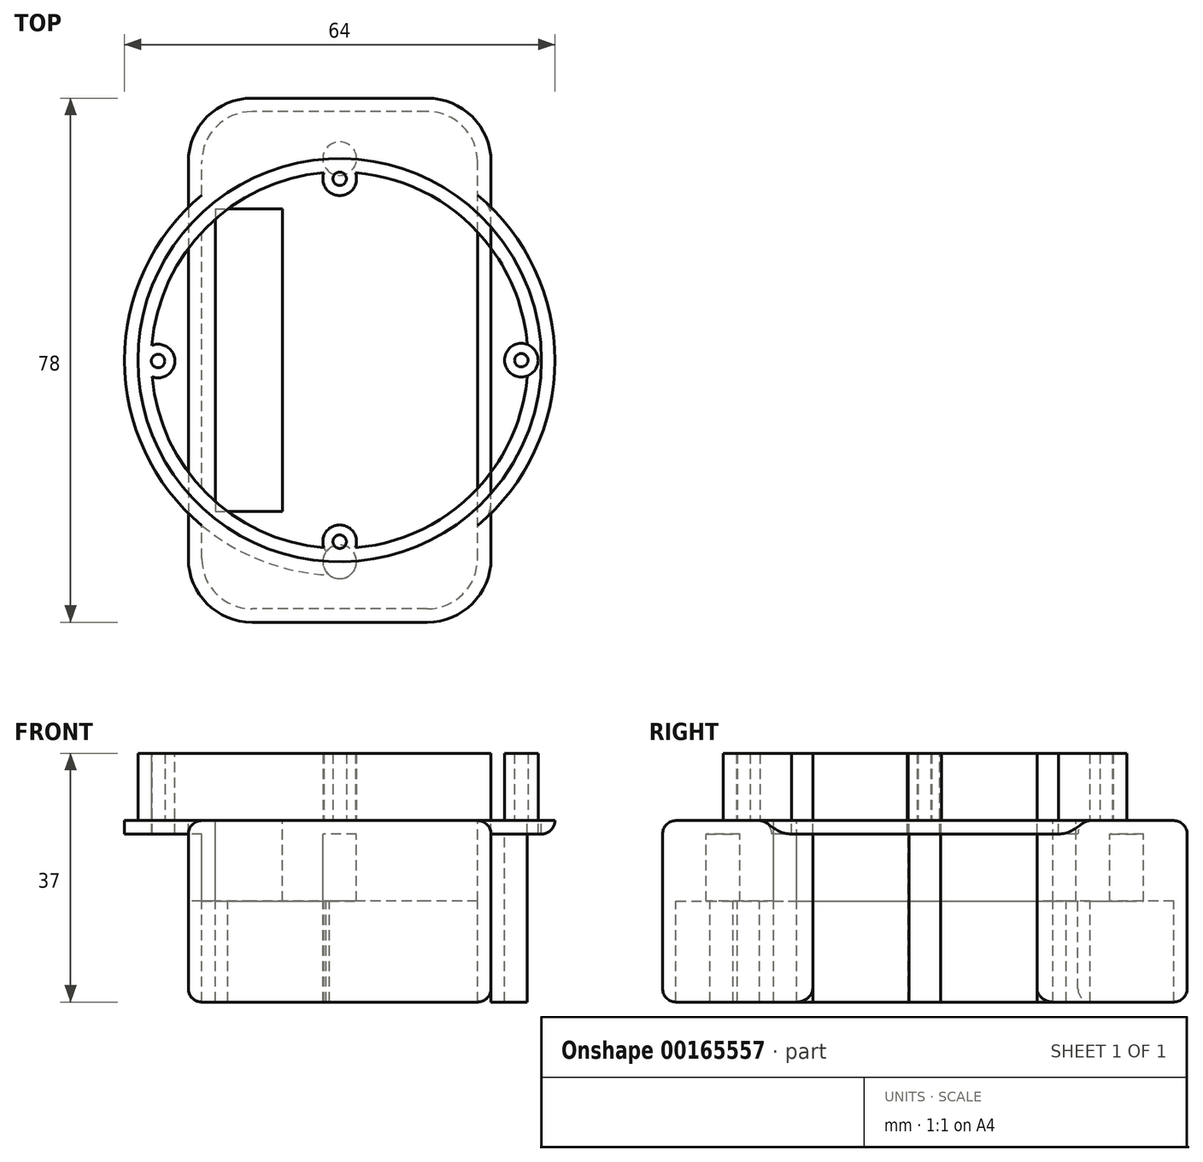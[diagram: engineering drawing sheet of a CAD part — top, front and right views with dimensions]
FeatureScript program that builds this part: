
annotation { "Feature Type Name" : "Feature", "Feature Type Description" : "" }
export const myFeature = defineFeature(function(context is Context, id is Id, definition is map)
    precondition{}
    {
        {
            var Q0;
            Q0=qCreatedBy(makeId("Top.planeOp"),FACE);
            var sketch = newSketch(context, id + "F0", { "sketchPlane" : qUnion([Q0])});
            skCircle(sketch, "E0", {"center": v(0, 0) * mm, "radius": 30 * mm});
            skCircle(sketch, "E1.0", {"center": v(0, 0) * mm, "radius": 28 * mm});
            skLineSegment(sketch, "E2.bottom", {"start": v(13, -37) * mm, "end": v(-13, -37) * mm});
            skLineSegment(sketch, "E2.top", {"start": v(13, 37) * mm, "end": v(-13, 37) * mm});
            skLineSegment(sketch, "E2.left", {"start": v(20.5, -29.5) * mm, "end": v(20.5, 29.5) * mm});
            skLineSegment(sketch, "E2.right", {"start": v(-20.5, -29.5) * mm, "end": v(-20.5, 29.5) * mm});
            skPoint(sketch, "E3.visualSharp", {"position": v(-20.5, 37) * mm});
            skArc(sketch, "E3.filletArc", {"start": v(-13, 37) * mm, "mid": v(-18.3, 34.8) * mm, "end": v(-20.5, 29.5) * mm});
            skPoint(sketch, "E4.visualSharp", {"position": v(20.5, 37) * mm});
            skArc(sketch, "E4.filletArc", {"start": v(20.5, 29.5) * mm, "mid": v(18.3, 34.8) * mm, "end": v(13, 37) * mm});
            skPoint(sketch, "E5.visualSharp", {"position": v(20.5, -37) * mm});
            skArc(sketch, "E5.filletArc", {"start": v(13, -37) * mm, "mid": v(18.3, -34.8) * mm, "end": v(20.5, -29.5) * mm});
            skPoint(sketch, "E6.visualSharp", {"position": v(-20.5, -37) * mm});
            skArc(sketch, "E6.filletArc", {"start": v(-20.5, -29.5) * mm, "mid": v(-18.3, -34.8) * mm, "end": v(-13, -37) * mm});
            skArc(sketch, "E7.0", {"start": v(-22.5, -29.5) * mm, "mid": v(-19.72, -36.22) * mm, "end": v(-13, -39) * mm});
            skLineSegment(sketch, "E7.1", {"start": v(13, -39) * mm, "end": v(-13, -39) * mm});
            skLineSegment(sketch, "E7.2", {"start": v(-22.5, -29.5) * mm, "end": v(-22.5, 29.5) * mm});
            skArc(sketch, "E7.3", {"start": v(13, -39) * mm, "mid": v(19.72, -36.22) * mm, "end": v(22.5, -29.5) * mm});
            skArc(sketch, "E7.4", {"start": v(-13, 39) * mm, "mid": v(-19.72, 36.22) * mm, "end": v(-22.5, 29.5) * mm});
            skLineSegment(sketch, "E7.5", {"start": v(13, 39) * mm, "end": v(-13, 39) * mm});
            skArc(sketch, "E7.6", {"start": v(22.5, 29.5) * mm, "mid": v(19.72, 36.22) * mm, "end": v(13, 39) * mm});
            skLineSegment(sketch, "E7.7", {"start": v(22.5, -29.5) * mm, "end": v(22.5, 29.5) * mm});
            skCircle(sketch, "E8", {"center": v(0, 0) * mm, "radius": 27 * mm, "construction": true});
            skCircle(sketch, "E9", {"center": v(0, -27) * mm, "radius": 2.5 * mm});
            skCircle(sketch, "E10", {"center": v(0, 27) * mm, "radius": 2.5 * mm});
            skCircle(sketch, "E11", {"center": v(-27, -0.12) * mm, "radius": 2.5 * mm});
            skCircle(sketch, "E12", {"center": v(27, 0) * mm, "radius": 2.5 * mm});
            skPoint(sketch, "E12.centerSnap0", {"position": v(20.5, 0) * mm});
            skCircle(sketch, "E13", {"center": v(-27, -0.12) * mm, "radius": 1 * mm});
            skCircle(sketch, "E14", {"center": v(0, 27) * mm, "radius": 1 * mm});
            skCircle(sketch, "E15", {"center": v(0, -27) * mm, "radius": 1 * mm});
            skCircle(sketch, "E16", {"center": v(27, 0) * mm, "radius": 1 * mm});
            skLineSegment(sketch, "E17.top", {"start": v(-18.5, 22.5) * mm, "end": v(-8.5, 22.5) * mm});
            skLineSegment(sketch, "E17.left", {"start": v(-18.5, 0) * mm, "end": v(-18.5, 22.5) * mm});
            skLineSegment(sketch, "E17.right", {"start": v(-8.5, 0) * mm, "end": v(-8.5, 22.5) * mm});
            skLineSegment(sketch, "E18.MirrorCS", {"start": v(-8.5, 0) * mm, "end": v(-8.5, -22.5) * mm});
            skLineSegment(sketch, "E19.MirrorCS", {"start": v(-18.5, 0) * mm, "end": v(-18.5, -22.5) * mm});
            skLineSegment(sketch, "E20.MirrorCS", {"start": v(-18.5, -22.5) * mm, "end": v(-8.5, -22.5) * mm});
            skLineSegment(sketch, "E21", {"start": v(0, 0) * mm, "end": v(0, -30) * mm});
            skCircle(sketch, "E22", {"center": v(0, -30) * mm, "radius": 2.5 * mm});
            skCircle(sketch, "E23", {"center": v(0, 30) * mm, "radius": 2.5 * mm});
            skCircle(sketch, "E24", {"center": v(0, 0) * mm, "radius": 32 * mm});
            skSolve(sketch);
        }
        {
            var Q0;
            {var subQ5=sQuery(id+"F0.wireOp",EDGE,"E17.right");Q0=makeQuery(id+"F0.imprint","IMPRINT",FACE,{"disambiguationData":[TD([[makeQuery(id+"F0.imprint","IMPRINT",EDGE,{"derivedFrom":subQ5}),-1.0]])]});}
            var Q1;
            Q1=makeQuery(id+"F0.imprint","IMPRINT",FACE,{"disambiguationData":[TD([[makeQuery(id+"F0.imprint","IMPRINT",EDGE,{"derivedFrom":sQuery(id+"F0.wireOp",EDGE,"E2.top")}),1.0]])]});
            var Q2;
            Q2=makeQuery(id+"F0.imprint","IMPRINT",FACE,{"disambiguationData":[TD([[makeQuery(id+"F0.imprint","IMPRINT",EDGE,{"derivedFrom":sQuery(id+"F0.wireOp",EDGE,"E2.bottom")}),-1.0]])]});
            var Q3;
            {var subQ1=sQuery(id+"F0.wireOp",EDGE,"E17.left");var subQ3=sQuery(id+"F0.wireOp",EDGE,"E1.0");var subQ4=makeQuery(id+"F0.imprint","INTERSECT",VERTEX,{"derivedFrom":[subQ3,subQ1]});Q3=makeQuery(id+"F0.imprint","IMPRINT",FACE,{"disambiguationData":[TD([[makeQuery(id+"F0.imprint","IMPRINT",EDGE,{"disambiguationData":[TD([[subQ4,-1.0]])],"derivedFrom":subQ3}),1.0]])]});}
            var Q4;
            {var subQ5=sQuery(id+"F0.wireOp",EDGE,"E2.right");var subQ6=sQuery(id+"F0.wireOp",EDGE,"E0");var subQ7=makeQuery(id+"F0.imprint","INTERSECT",VERTEX,{"disambiguationData":[OD(1.0)],"derivedFrom":[subQ6,subQ5]});Q4=makeQuery(id+"F0.imprint","IMPRINT",FACE,{"disambiguationData":[TD([[makeQuery(id+"F0.imprint","IMPRINT",EDGE,{"disambiguationData":[TD([[subQ7,-1.0]])],"derivedFrom":subQ6}),1.0]])]});}
            var Q5;
            {var subQ6=sQuery(id+"F0.wireOp",EDGE,"E0");var subQ11=sQuery(id+"F0.wireOp",EDGE,"E23");var subQ12=makeQuery(id+"F0.imprint","INTERSECT",VERTEX,{"disambiguationData":[OD(1.0)],"derivedFrom":[subQ6,subQ11]});Q5=makeQuery(id+"F0.imprint","IMPRINT",FACE,{"disambiguationData":[TD([[makeQuery(id+"F0.imprint","IMPRINT",EDGE,{"disambiguationData":[TD([[subQ12,-1.0]])],"derivedFrom":subQ6}),1.0]])]});}
            var Q6;
            {var subQ0=sQuery(id+"F0.wireOp",EDGE,"E10");var subQ1=sQuery(id+"F0.wireOp",EDGE,"E1.0");var subQ2=makeQuery(id+"F0.imprint","INTERSECT",VERTEX,{"disambiguationData":[OD(0.0)],"derivedFrom":[subQ1,subQ0]});Q6=makeQuery(id+"F0.imprint","IMPRINT",FACE,{"disambiguationData":[TD([[makeQuery(id+"F0.imprint","IMPRINT",EDGE,{"disambiguationData":[TD([[subQ2,-1.0]])],"derivedFrom":subQ1}),1.0]])]});}
            var Q7;
            {var subQ0=sQuery(id+"F0.wireOp",EDGE,"E23");var subQ1=sQuery(id+"F0.wireOp",EDGE,"E14");var subQ2=makeQuery(id+"F0.imprint","INTERSECT",VERTEX,{"disambiguationData":[OD(0.0)],"derivedFrom":[subQ1,subQ0]});Q7=makeQuery(id+"F0.imprint","IMPRINT",FACE,{"disambiguationData":[TD([[makeQuery(id+"F0.imprint","IMPRINT",EDGE,{"disambiguationData":[TD([[subQ2,1.0]])],"derivedFrom":subQ1}),1.0]])]});}
            var Q8;
            {var subQ0=sQuery(id+"F0.wireOp",EDGE,"E23");var subQ1=sQuery(id+"F0.wireOp",EDGE,"E1.0");var subQ2=makeQuery(id+"F0.imprint","INTERSECT",VERTEX,{"disambiguationData":[OD(1.0)],"derivedFrom":[subQ1,subQ0]});Q8=makeQuery(id+"F0.imprint","IMPRINT",FACE,{"disambiguationData":[TD([[makeQuery(id+"F0.imprint","IMPRINT",EDGE,{"disambiguationData":[TD([[subQ2,-1.0]])],"derivedFrom":subQ1}),-1.0]])]});}
            var Q9;
            {var subQ0=sQuery(id+"F0.wireOp",EDGE,"E10");var subQ1=sQuery(id+"F0.wireOp",EDGE,"E1.0");var subQ2=makeQuery(id+"F0.imprint","INTERSECT",VERTEX,{"disambiguationData":[OD(0.0)],"derivedFrom":[subQ1,subQ0]});Q9=makeQuery(id+"F0.imprint","IMPRINT",FACE,{"disambiguationData":[TD([[makeQuery(id+"F0.imprint","IMPRINT",EDGE,{"disambiguationData":[TD([[subQ2,-1.0]])],"derivedFrom":subQ1}),-1.0]])]});}
            var Q10;
            {var subQ0=sQuery(id+"F0.wireOp",EDGE,"E23");var subQ1=sQuery(id+"F0.wireOp",EDGE,"E0");var subQ2=makeQuery(id+"F0.imprint","INTERSECT",VERTEX,{"disambiguationData":[OD(1.0)],"derivedFrom":[subQ1,subQ0]});Q10=makeQuery(id+"F0.imprint","IMPRINT",FACE,{"disambiguationData":[TD([[makeQuery(id+"F0.imprint","IMPRINT",EDGE,{"disambiguationData":[TD([[subQ2,-1.0]])],"derivedFrom":subQ1}),-1.0]])]});}
            var Q11;
            {var subQ0=sQuery(id+"F0.wireOp",EDGE,"E2.left");var subQ1=sQuery(id+"F0.wireOp",EDGE,"E0");var subQ2=makeQuery(id+"F0.imprint","INTERSECT",VERTEX,{"disambiguationData":[OD(0.0)],"derivedFrom":[subQ1,subQ0]});Q11=makeQuery(id+"F0.imprint","IMPRINT",FACE,{"disambiguationData":[TD([[makeQuery(id+"F0.imprint","IMPRINT",EDGE,{"disambiguationData":[TD([[subQ2,-1.0]])],"derivedFrom":subQ1}),-1.0]])]});}
            var Q12;
            {var subQ5=sQuery(id+"F0.wireOp",EDGE,"E2.left");var subQ6=sQuery(id+"F0.wireOp",EDGE,"E0");var subQ7=makeQuery(id+"F0.imprint","INTERSECT",VERTEX,{"disambiguationData":[OD(0.0)],"derivedFrom":[subQ6,subQ5]});Q12=makeQuery(id+"F0.imprint","IMPRINT",FACE,{"disambiguationData":[TD([[makeQuery(id+"F0.imprint","IMPRINT",EDGE,{"disambiguationData":[TD([[subQ7,-1.0]])],"derivedFrom":subQ6}),1.0]])]});}
            var Q13;
            {var subQ0=sQuery(id+"F0.wireOp",EDGE,"E22");var subQ1=sQuery(id+"F0.wireOp",EDGE,"E0");var subQ2=makeQuery(id+"F0.imprint","INTERSECT",VERTEX,{"disambiguationData":[OD(1.0)],"derivedFrom":[subQ1,subQ0]});Q13=makeQuery(id+"F0.imprint","IMPRINT",FACE,{"disambiguationData":[TD([[makeQuery(id+"F0.imprint","IMPRINT",EDGE,{"disambiguationData":[TD([[subQ2,-1.0]])],"derivedFrom":subQ1}),-1.0]])]});}
            var Q14;
            {var subQ3=sQuery(id+"F0.wireOp",EDGE,"E22");var subQ6=sQuery(id+"F0.wireOp",EDGE,"E0");var subQ9=makeQuery(id+"F0.imprint","INTERSECT",VERTEX,{"disambiguationData":[OD(1.0)],"derivedFrom":[subQ6,subQ3]});Q14=makeQuery(id+"F0.imprint","IMPRINT",FACE,{"disambiguationData":[TD([[makeQuery(id+"F0.imprint","IMPRINT",EDGE,{"disambiguationData":[TD([[subQ9,-1.0]])],"derivedFrom":subQ6}),1.0]])]});}
            var Q15;
            {var subQ5=sQuery(id+"F0.wireOp",EDGE,"E1.0");var subQ7=sQuery(id+"F0.wireOp",EDGE,"E22");var subQ9=makeQuery(id+"F0.imprint","INTERSECT",VERTEX,{"disambiguationData":[OD(1.0)],"derivedFrom":[subQ5,subQ7]});Q15=makeQuery(id+"F0.imprint","IMPRINT",FACE,{"disambiguationData":[TD([[makeQuery(id+"F0.imprint","IMPRINT",EDGE,{"disambiguationData":[TD([[subQ9,-1.0]])],"derivedFrom":subQ5}),1.0]])]});}
            var Q16;
            {var subQ0=sQuery(id+"F0.wireOp",EDGE,"E2.right");var subQ1=sQuery(id+"F0.wireOp",EDGE,"E0");var subQ2=makeQuery(id+"F0.imprint","INTERSECT",VERTEX,{"disambiguationData":[OD(1.0)],"derivedFrom":[subQ1,subQ0]});Q16=makeQuery(id+"F0.imprint","IMPRINT",FACE,{"disambiguationData":[TD([[makeQuery(id+"F0.imprint","IMPRINT",EDGE,{"disambiguationData":[TD([[subQ2,-1.0]])],"derivedFrom":subQ1}),-1.0]])]});}
            var Q17;
            {var subQ0=sQuery(id+"F0.wireOp",EDGE,"E22");var subQ1=sQuery(id+"F0.wireOp",EDGE,"E1.0");var subQ2=makeQuery(id+"F0.imprint","INTERSECT",VERTEX,{"disambiguationData":[OD(1.0)],"derivedFrom":[subQ1,subQ0]});Q17=makeQuery(id+"F0.imprint","IMPRINT",FACE,{"disambiguationData":[TD([[makeQuery(id+"F0.imprint","IMPRINT",EDGE,{"disambiguationData":[TD([[subQ2,-1.0]])],"derivedFrom":subQ1}),-1.0]])]});}
            var Q18;
            {var subQ0=sQuery(id+"F0.wireOp",EDGE,"E9");var subQ1=sQuery(id+"F0.wireOp",EDGE,"E1.0");var subQ2=makeQuery(id+"F0.imprint","INTERSECT",VERTEX,{"disambiguationData":[OD(0.0)],"derivedFrom":[subQ1,subQ0]});Q18=makeQuery(id+"F0.imprint","IMPRINT",FACE,{"disambiguationData":[TD([[makeQuery(id+"F0.imprint","IMPRINT",EDGE,{"disambiguationData":[TD([[subQ2,-1.0]])],"derivedFrom":subQ1}),-1.0]])]});}
            var Q19;
            {var subQ1=sQuery(id+"F0.wireOp",EDGE,"E9");var subQ3=sQuery(id+"F0.wireOp",EDGE,"E1.0");var subQ4=makeQuery(id+"F0.imprint","INTERSECT",VERTEX,{"disambiguationData":[OD(0.0)],"derivedFrom":[subQ3,subQ1]});Q19=makeQuery(id+"F0.imprint","IMPRINT",FACE,{"disambiguationData":[TD([[makeQuery(id+"F0.imprint","IMPRINT",EDGE,{"disambiguationData":[TD([[subQ4,-1.0]])],"derivedFrom":subQ3}),1.0]])]});}
            var Q20;
            {var subQ0=sQuery(id+"F0.wireOp",EDGE,"E22");var subQ1=sQuery(id+"F0.wireOp",EDGE,"E15");var subQ2=makeQuery(id+"F0.imprint","INTERSECT",VERTEX,{"disambiguationData":[OD(0.0)],"derivedFrom":[subQ1,subQ0]});Q20=makeQuery(id+"F0.imprint","IMPRINT",FACE,{"disambiguationData":[TD([[makeQuery(id+"F0.imprint","IMPRINT",EDGE,{"disambiguationData":[TD([[subQ2,1.0]])],"derivedFrom":subQ1}),1.0]])]});}
            var Q21;
            {var subQ0=sQuery(id+"F0.wireOp",EDGE,"E21");var subQ1=sQuery(id+"F0.wireOp",EDGE,"E15");var subQ2=makeQuery(id+"F0.imprint","INTERSECT",VERTEX,{"derivedFrom":[subQ1,subQ0]});Q21=makeQuery(id+"F0.imprint","IMPRINT",FACE,{"disambiguationData":[TD([[makeQuery(id+"F0.imprint","IMPRINT",EDGE,{"disambiguationData":[TD([[subQ2,1.0]])],"derivedFrom":subQ1}),1.0]])]});}
            extrude(context, id + "F1", {"entities" : qUnion([Q0, Q1, Q2, Q3, Q4, Q5, Q6, Q7, Q8, Q9, Q10, Q11, Q12, Q13, Q14, Q15, Q16, Q17, Q18, Q19, Q20, Q21]), "oppositeDirection" : true, "depth" : 2 * mm});
        }
        {
            var Q0;
            Q0=makeQuery(id+"F0.imprint","IMPRINT",FACE,{"disambiguationData":[TD([[makeQuery(id+"F0.imprint","IMPRINT",EDGE,{"derivedFrom":sQuery(id+"F0.wireOp",EDGE,"E2.top")}),-1.0]])]});
            var Q1;
            {var subQ0=sQuery(id+"F0.wireOp",EDGE,"E7.7");var subQ1=sQuery(id+"F0.wireOp",EDGE,"E1.0");var subQ2=makeQuery(id+"F0.imprint","INTERSECT",VERTEX,{"disambiguationData":[OD(0.0)],"derivedFrom":[subQ1,subQ0]});Q1=makeQuery(id+"F0.imprint","IMPRINT",FACE,{"disambiguationData":[TD([[makeQuery(id+"F0.imprint","IMPRINT",EDGE,{"disambiguationData":[TD([[subQ2,-1.0]])],"derivedFrom":subQ1}),1.0]])]});}
            var Q2;
            {var subQ0=sQuery(id+"F0.wireOp",EDGE,"E2.left");var subQ1=sQuery(id+"F0.wireOp",EDGE,"E0");var subQ2=makeQuery(id+"F0.imprint","INTERSECT",VERTEX,{"disambiguationData":[OD(0.0)],"derivedFrom":[subQ1,subQ0]});Q2=makeQuery(id+"F0.imprint","IMPRINT",FACE,{"disambiguationData":[TD([[makeQuery(id+"F0.imprint","IMPRINT",EDGE,{"disambiguationData":[TD([[subQ2,1.0]])],"derivedFrom":subQ1}),1.0]])]});}
            var Q3;
            {var subQ0=sQuery(id+"F0.wireOp",EDGE,"E2.left");var subQ1=sQuery(id+"F0.wireOp",EDGE,"E0");var subQ2=makeQuery(id+"F0.imprint","INTERSECT",VERTEX,{"disambiguationData":[OD(0.0)],"derivedFrom":[subQ1,subQ0]});Q3=makeQuery(id+"F0.imprint","IMPRINT",FACE,{"disambiguationData":[TD([[makeQuery(id+"F0.imprint","IMPRINT",EDGE,{"disambiguationData":[TD([[subQ2,1.0]])],"derivedFrom":subQ1}),-1.0]])]});}
            var Q4;
            {var subQ0=sQuery(id+"F0.wireOp",EDGE,"E2.left");var subQ1=sQuery(id+"F0.wireOp",EDGE,"E0");var subQ2=makeQuery(id+"F0.imprint","INTERSECT",VERTEX,{"disambiguationData":[OD(1.0)],"derivedFrom":[subQ1,subQ0]});Q4=makeQuery(id+"F0.imprint","IMPRINT",FACE,{"disambiguationData":[TD([[makeQuery(id+"F0.imprint","IMPRINT",EDGE,{"disambiguationData":[TD([[subQ2,-1.0]])],"derivedFrom":subQ1}),1.0]])]});}
            var Q5;
            {var subQ0=sQuery(id+"F0.wireOp",EDGE,"E2.left");var subQ1=sQuery(id+"F0.wireOp",EDGE,"E0");var subQ2=makeQuery(id+"F0.imprint","INTERSECT",VERTEX,{"disambiguationData":[OD(1.0)],"derivedFrom":[subQ1,subQ0]});Q5=makeQuery(id+"F0.imprint","IMPRINT",FACE,{"disambiguationData":[TD([[makeQuery(id+"F0.imprint","IMPRINT",EDGE,{"disambiguationData":[TD([[subQ2,-1.0]])],"derivedFrom":subQ1}),-1.0]])]});}
            var Q6;
            Q6=makeQuery(id+"F0.imprint","IMPRINT",FACE,{"disambiguationData":[TD([[makeQuery(id+"F0.imprint","IMPRINT",EDGE,{"derivedFrom":sQuery(id+"F0.wireOp",EDGE,"E2.bottom")}),1.0]])]});
            var Q7;
            {var subQ0=sQuery(id+"F0.wireOp",EDGE,"E2.right");var subQ1=sQuery(id+"F0.wireOp",EDGE,"E1.0");var subQ2=makeQuery(id+"F0.imprint","INTERSECT",VERTEX,{"disambiguationData":[OD(0.0)],"derivedFrom":[subQ1,subQ0]});Q7=makeQuery(id+"F0.imprint","IMPRINT",FACE,{"disambiguationData":[TD([[makeQuery(id+"F0.imprint","IMPRINT",EDGE,{"disambiguationData":[TD([[subQ2,-1.0]])],"derivedFrom":subQ1}),1.0]])]});}
            var Q8;
            {var subQ0=sQuery(id+"F0.wireOp",EDGE,"E7.2");var subQ1=sQuery(id+"F0.wireOp",EDGE,"E0");var subQ2=makeQuery(id+"F0.imprint","INTERSECT",VERTEX,{"disambiguationData":[OD(1.0)],"derivedFrom":[subQ1,subQ0]});Q8=makeQuery(id+"F0.imprint","IMPRINT",FACE,{"disambiguationData":[TD([[makeQuery(id+"F0.imprint","IMPRINT",EDGE,{"disambiguationData":[TD([[subQ2,-1.0]])],"derivedFrom":subQ1}),1.0]])]});}
            var Q9;
            {var subQ0=sQuery(id+"F0.wireOp",EDGE,"E7.2");var subQ1=sQuery(id+"F0.wireOp",EDGE,"E0");var subQ2=makeQuery(id+"F0.imprint","INTERSECT",VERTEX,{"disambiguationData":[OD(1.0)],"derivedFrom":[subQ1,subQ0]});Q9=makeQuery(id+"F0.imprint","IMPRINT",FACE,{"disambiguationData":[TD([[makeQuery(id+"F0.imprint","IMPRINT",EDGE,{"disambiguationData":[TD([[subQ2,-1.0]])],"derivedFrom":subQ1}),-1.0]])]});}
            var Q10;
            {var subQ0=sQuery(id+"F0.wireOp",EDGE,"E2.right");var subQ1=sQuery(id+"F0.wireOp",EDGE,"E0");var subQ2=makeQuery(id+"F0.imprint","INTERSECT",VERTEX,{"disambiguationData":[OD(0.0)],"derivedFrom":[subQ1,subQ0]});Q10=makeQuery(id+"F0.imprint","IMPRINT",FACE,{"disambiguationData":[TD([[makeQuery(id+"F0.imprint","IMPRINT",EDGE,{"disambiguationData":[TD([[subQ2,-1.0]])],"derivedFrom":subQ1}),-1.0]])]});}
            var Q11;
            {var subQ0=sQuery(id+"F0.wireOp",EDGE,"E2.right");var subQ1=sQuery(id+"F0.wireOp",EDGE,"E0");var subQ2=makeQuery(id+"F0.imprint","INTERSECT",VERTEX,{"disambiguationData":[OD(0.0)],"derivedFrom":[subQ1,subQ0]});Q11=makeQuery(id+"F0.imprint","IMPRINT",FACE,{"disambiguationData":[TD([[makeQuery(id+"F0.imprint","IMPRINT",EDGE,{"disambiguationData":[TD([[subQ2,-1.0]])],"derivedFrom":subQ1}),1.0]])]});}
            extrude(context, id + "F2", {"entities" : qUnion([Q0, Q1, Q2, Q3, Q4, Q5, Q6, Q7, Q8, Q9, Q10, Q11]), "operationType" : NewBodyOperationType.ADD, "oppositeDirection" : true, "depth" : 27 * mm});
        }
        {
            var Q0;
            Q0=makeQuery(id+"F1.opExtrude","CAP_FACE",FACE,{"disambiguationData":[OSD([sQuery(id+"F0.wireOp",EDGE,"E2.bottom"),sQuery(id+"F0.wireOp",EDGE,"E2.top"),sQuery(id+"F0.wireOp",EDGE,"E2.left"),sQuery(id+"F0.wireOp",EDGE,"E2.right"),sQuery(id+"F0.wireOp",EDGE,"E3.filletArc"),sQuery(id+"F0.wireOp",EDGE,"E4.filletArc"),sQuery(id+"F0.wireOp",EDGE,"E5.filletArc"),sQuery(id+"F0.wireOp",EDGE,"E6.filletArc"),sQuery(id+"F0.wireOp",EDGE,"E17.top"),sQuery(id+"F0.wireOp",EDGE,"E17.left"),sQuery(id+"F0.wireOp",EDGE,"E17.right"),sQuery(id+"F0.wireOp",EDGE,"E19.MirrorCS"),sQuery(id+"F0.wireOp",EDGE,"E20.MirrorCS"),sQuery(id+"F0.wireOp",EDGE,"E18.MirrorCS")])],"isStart":false});
            extrude(context, id + "F3", {"entities" : qUnion([Q0]), "operationType" : NewBodyOperationType.ADD, "depth" : 10 * mm});
        }
        {
            var Q0;
            Q0=qSketchRegion(id+"F0",true);
            var Q1;
            {var subQ3=sQuery(id+"F0.wireOp",EDGE,"E7.2");var subQ7=sQuery(id+"F0.wireOp",EDGE,"E0");var subQ9=makeQuery(id+"F0.imprint","INTERSECT",VERTEX,{"disambiguationData":[OD(0.0)],"derivedFrom":[subQ7,subQ3]});Q1=makeQuery(id+"F0.imprint","IMPRINT",FACE,{"disambiguationData":[TD([[makeQuery(id+"F0.imprint","IMPRINT",EDGE,{"disambiguationData":[TD([[subQ9,-1.0]])],"derivedFrom":subQ7}),1.0]])]});}
            var Q2;
            {var subQ0=sQuery(id+"F0.wireOp",EDGE,"E7.2");var subQ1=sQuery(id+"F0.wireOp",EDGE,"E1.0");var subQ2=makeQuery(id+"F0.imprint","INTERSECT",VERTEX,{"disambiguationData":[OD(0.0)],"derivedFrom":[subQ1,subQ0]});Q2=makeQuery(id+"F0.imprint","IMPRINT",FACE,{"disambiguationData":[TD([[makeQuery(id+"F0.imprint","IMPRINT",EDGE,{"disambiguationData":[TD([[subQ2,-1.0]])],"derivedFrom":subQ1}),1.0]])]});}
            var Q3;
            {var subQ0=sQuery(id+"F0.wireOp",EDGE,"E13");Q3=makeQuery(id+"F0.imprint","IMPRINT",FACE,{"disambiguationData":[TD([[makeQuery(id+"F0.imprint","IMPRINT",EDGE,{"derivedFrom":subQ0}),-1.0]])]});}
            var Q4;
            {var subQ0=sQuery(id+"F0.wireOp",EDGE,"E1.0");var subQ1=makeQuery(id+"F0.imprint","INTERSECT",VERTEX,{"derivedFrom":[subQ0,sQuery(id+"F0.wireOp",EDGE,"E13")]});Q4=makeQuery(id+"F0.imprint","IMPRINT",FACE,{"disambiguationData":[TD([[makeQuery(id+"F0.imprint","IMPRINT",EDGE,{"disambiguationData":[TD([[subQ1,1.0]])],"derivedFrom":subQ0}),-1.0]])]});}
            var Q5;
            Q5=makeQuery(id+"F0.imprint","IMPRINT",FACE,{"disambiguationData":[TD([[makeQuery(id+"F0.imprint","IMPRINT",EDGE,{"derivedFrom":sQuery(id+"F0.wireOp",EDGE,"E13")}),1.0]])]});
            var Q6;
            {var subQ0=sQuery(id+"F0.wireOp",EDGE,"E12");var subQ1=sQuery(id+"F0.wireOp",EDGE,"E1.0");var subQ2=makeQuery(id+"F0.imprint","INTERSECT",VERTEX,{"disambiguationData":[OD(0.0)],"derivedFrom":[subQ1,subQ0]});Q6=makeQuery(id+"F0.imprint","IMPRINT",FACE,{"disambiguationData":[TD([[makeQuery(id+"F0.imprint","IMPRINT",EDGE,{"disambiguationData":[TD([[subQ2,-1.0]])],"derivedFrom":subQ1}),1.0]])]});}
            var Q7;
            {var subQ0=sQuery(id+"F0.wireOp",EDGE,"E16");Q7=makeQuery(id+"F0.imprint","IMPRINT",FACE,{"disambiguationData":[TD([[makeQuery(id+"F0.imprint","IMPRINT",EDGE,{"derivedFrom":subQ0}),-1.0]])]});}
            var Q8;
            Q8=makeQuery(id+"F0.imprint","IMPRINT",FACE,{"disambiguationData":[TD([[makeQuery(id+"F0.imprint","IMPRINT",EDGE,{"derivedFrom":sQuery(id+"F0.wireOp",EDGE,"E16")}),1.0]])]});
            var Q9;
            {var subQ0=sQuery(id+"F0.wireOp",EDGE,"E7.7");var subQ1=sQuery(id+"F0.wireOp",EDGE,"E0");var subQ9=makeQuery(id+"F0.imprint","INTERSECT",VERTEX,{"disambiguationData":[OD(0.0)],"derivedFrom":[subQ1,subQ0]});Q9=makeQuery(id+"F0.imprint","IMPRINT",FACE,{"disambiguationData":[TD([[makeQuery(id+"F0.imprint","IMPRINT",EDGE,{"disambiguationData":[TD([[subQ9,1.0]])],"derivedFrom":subQ1}),1.0]])]});}
            var Q10;
            {var subQ0=sQuery(id+"F0.wireOp",EDGE,"E1.0");var subQ1=makeQuery(id+"F0.imprint","INTERSECT",VERTEX,{"derivedFrom":[subQ0,sQuery(id+"F0.wireOp",EDGE,"E16")]});Q10=makeQuery(id+"F0.imprint","IMPRINT",FACE,{"disambiguationData":[TD([[makeQuery(id+"F0.imprint","IMPRINT",EDGE,{"disambiguationData":[TD([[subQ1,-1.0]])],"derivedFrom":subQ0}),-1.0]])]});}
            var Q11;
            {var subQ0=sQuery(id+"F0.wireOp",EDGE,"E23");var subQ1=sQuery(id+"F0.wireOp",EDGE,"E0");var subQ2=makeQuery(id+"F0.imprint","INTERSECT",VERTEX,{"disambiguationData":[OD(0.0)],"derivedFrom":[subQ1,subQ0]});Q11=makeQuery(id+"F0.imprint","IMPRINT",FACE,{"disambiguationData":[TD([[makeQuery(id+"F0.imprint","IMPRINT",EDGE,{"disambiguationData":[TD([[subQ2,-1.0]])],"derivedFrom":subQ1}),-1.0]])]});}
            var Q12;
            {var subQ0=sQuery(id+"F0.wireOp",EDGE,"E24");var subQ1=sQuery(id+"F0.wireOp",EDGE,"E23");var subQ2=makeQuery(id+"F0.imprint","INTERSECT",VERTEX,{"disambiguationData":[OD(0.0)],"derivedFrom":[subQ1,subQ0]});Q12=makeQuery(id+"F0.imprint","IMPRINT",FACE,{"disambiguationData":[TD([[makeQuery(id+"F0.imprint","IMPRINT",EDGE,{"disambiguationData":[TD([[subQ2,1.0]])],"derivedFrom":subQ1}),1.0]])]});}
            var Q13;
            {var subQ0=sQuery(id+"F0.wireOp",EDGE,"E23");var subQ1=sQuery(id+"F0.wireOp",EDGE,"E0");var subQ2=makeQuery(id+"F0.imprint","INTERSECT",VERTEX,{"disambiguationData":[OD(0.0)],"derivedFrom":[subQ1,subQ0]});Q13=makeQuery(id+"F0.imprint","IMPRINT",FACE,{"disambiguationData":[TD([[makeQuery(id+"F0.imprint","IMPRINT",EDGE,{"disambiguationData":[TD([[subQ2,-1.0]])],"derivedFrom":subQ1}),1.0]])]});}
            var Q14;
            {var subQ0=sQuery(id+"F0.wireOp",EDGE,"E23");var subQ4=sQuery(id+"F0.wireOp",EDGE,"E1.0");var subQ7=makeQuery(id+"F0.imprint","INTERSECT",VERTEX,{"disambiguationData":[OD(0.0)],"derivedFrom":[subQ4,subQ0]});Q14=makeQuery(id+"F0.imprint","IMPRINT",FACE,{"disambiguationData":[TD([[makeQuery(id+"F0.imprint","IMPRINT",EDGE,{"disambiguationData":[TD([[subQ7,-1.0]])],"derivedFrom":subQ4}),-1.0]])]});}
            var Q15;
            {var subQ0=sQuery(id+"F0.wireOp",EDGE,"E23");var subQ1=sQuery(id+"F0.wireOp",EDGE,"E1.0");var subQ2=makeQuery(id+"F0.imprint","INTERSECT",VERTEX,{"disambiguationData":[OD(0.0)],"derivedFrom":[subQ1,subQ0]});Q15=makeQuery(id+"F0.imprint","IMPRINT",FACE,{"disambiguationData":[TD([[makeQuery(id+"F0.imprint","IMPRINT",EDGE,{"disambiguationData":[TD([[subQ2,-1.0]])],"derivedFrom":subQ1}),1.0]])]});}
            var Q16;
            {var subQ0=sQuery(id+"F0.wireOp",EDGE,"E14");var subQ1=makeQuery(id+"F0.imprint","INTERSECT",VERTEX,{"derivedFrom":[sQuery(id+"F0.wireOp",EDGE,"E1.0"),subQ0]});Q16=makeQuery(id+"F0.imprint","IMPRINT",FACE,{"disambiguationData":[TD([[makeQuery(id+"F0.imprint","IMPRINT",EDGE,{"disambiguationData":[TD([[subQ1,1.0]])],"derivedFrom":subQ0}),1.0]])]});}
            var Q17;
            {var subQ0=sQuery(id+"F0.wireOp",EDGE,"E14");var subQ1=sQuery(id+"F0.wireOp",EDGE,"E1.0");var subQ2=makeQuery(id+"F0.imprint","INTERSECT",VERTEX,{"derivedFrom":[subQ1,subQ0]});Q17=makeQuery(id+"F0.imprint","IMPRINT",FACE,{"disambiguationData":[TD([[makeQuery(id+"F0.imprint","IMPRINT",EDGE,{"disambiguationData":[TD([[subQ2,-1.0]])],"derivedFrom":subQ1}),1.0]])]});}
            var Q18;
            {var subQ0=sQuery(id+"F0.wireOp",EDGE,"E21");var subQ1=sQuery(id+"F0.wireOp",EDGE,"E0");var subQ2=makeQuery(id+"F0.imprint","INTERSECT",VERTEX,{"derivedFrom":[subQ1,subQ0]});Q18=makeQuery(id+"F0.imprint","IMPRINT",FACE,{"disambiguationData":[TD([[makeQuery(id+"F0.imprint","IMPRINT",EDGE,{"disambiguationData":[TD([[subQ2,-1.0]])],"derivedFrom":subQ1}),1.0]])]});}
            var Q19;
            {var subQ3=sQuery(id+"F0.wireOp",EDGE,"E21");var subQ5=sQuery(id+"F0.wireOp",EDGE,"E9");var subQ6=makeQuery(id+"F0.imprint","INTERSECT",VERTEX,{"disambiguationData":[OD(1.0)],"derivedFrom":[subQ5,subQ3]});Q19=makeQuery(id+"F0.imprint","IMPRINT",FACE,{"disambiguationData":[TD([[makeQuery(id+"F0.imprint","IMPRINT",EDGE,{"disambiguationData":[TD([[subQ6,-1.0]])],"derivedFrom":subQ5}),1.0]])]});}
            var Q20;
            {var subQ1=sQuery(id+"F0.wireOp",EDGE,"E0");var subQ7=makeQuery(id+"F0.imprint","INTERSECT",VERTEX,{"derivedFrom":[subQ1,sQuery(id+"F0.wireOp",EDGE,"E21")]});Q20=makeQuery(id+"F0.imprint","IMPRINT",FACE,{"disambiguationData":[TD([[makeQuery(id+"F0.imprint","IMPRINT",EDGE,{"disambiguationData":[TD([[subQ7,1.0]])],"derivedFrom":subQ1}),-1.0]])]});}
            var Q21;
            {var subQ0=sQuery(id+"F0.wireOp",EDGE,"E24");var subQ1=sQuery(id+"F0.wireOp",EDGE,"E22");var subQ2=makeQuery(id+"F0.imprint","INTERSECT",VERTEX,{"disambiguationData":[OD(0.0)],"derivedFrom":[subQ1,subQ0]});Q21=makeQuery(id+"F0.imprint","IMPRINT",FACE,{"disambiguationData":[TD([[makeQuery(id+"F0.imprint","IMPRINT",EDGE,{"disambiguationData":[TD([[subQ2,-1.0]])],"derivedFrom":subQ1}),1.0]])]});}
            var Q22;
            {var subQ0=sQuery(id+"F0.wireOp",EDGE,"E21");var subQ1=sQuery(id+"F0.wireOp",EDGE,"E0");var subQ2=makeQuery(id+"F0.imprint","INTERSECT",VERTEX,{"derivedFrom":[subQ1,subQ0]});Q22=makeQuery(id+"F0.imprint","IMPRINT",FACE,{"disambiguationData":[TD([[makeQuery(id+"F0.imprint","IMPRINT",EDGE,{"disambiguationData":[TD([[subQ2,1.0]])],"derivedFrom":subQ1}),1.0]])]});}
            var Q23;
            {var subQ0=sQuery(id+"F0.wireOp",EDGE,"E22");var subQ5=sQuery(id+"F0.wireOp",EDGE,"E9");var subQ7=makeQuery(id+"F0.imprint","INTERSECT",VERTEX,{"disambiguationData":[OD(0.0)],"derivedFrom":[subQ5,subQ0]});Q23=makeQuery(id+"F0.imprint","IMPRINT",FACE,{"disambiguationData":[TD([[makeQuery(id+"F0.imprint","IMPRINT",EDGE,{"disambiguationData":[TD([[subQ7,-1.0]])],"derivedFrom":subQ5}),1.0]])]});}
            var Q24;
            {var subQ0=sQuery(id+"F0.wireOp",EDGE,"E22");var subQ1=sQuery(id+"F0.wireOp",EDGE,"E15");var subQ2=makeQuery(id+"F0.imprint","INTERSECT",VERTEX,{"disambiguationData":[OD(0.0)],"derivedFrom":[subQ1,subQ0]});Q24=makeQuery(id+"F0.imprint","IMPRINT",FACE,{"disambiguationData":[TD([[makeQuery(id+"F0.imprint","IMPRINT",EDGE,{"disambiguationData":[TD([[subQ2,1.0]])],"derivedFrom":subQ0}),1.0]])]});}
            var Q25;
            {var subQ0=sQuery(id+"F0.wireOp",EDGE,"E22");var subQ1=sQuery(id+"F0.wireOp",EDGE,"E15");var subQ2=makeQuery(id+"F0.imprint","INTERSECT",VERTEX,{"disambiguationData":[OD(1.0)],"derivedFrom":[subQ1,subQ0]});Q25=makeQuery(id+"F0.imprint","IMPRINT",FACE,{"disambiguationData":[TD([[makeQuery(id+"F0.imprint","IMPRINT",EDGE,{"disambiguationData":[TD([[subQ2,-1.0]])],"derivedFrom":subQ0}),1.0]])]});}
            var Q26;
            {var subQ0=sQuery(id+"F0.wireOp",EDGE,"E22");var subQ1=sQuery(id+"F0.wireOp",EDGE,"E1.0");var subQ2=makeQuery(id+"F0.imprint","INTERSECT",VERTEX,{"disambiguationData":[OD(1.0)],"derivedFrom":[subQ1,subQ0]});Q26=makeQuery(id+"F0.imprint","IMPRINT",FACE,{"disambiguationData":[TD([[makeQuery(id+"F0.imprint","IMPRINT",EDGE,{"disambiguationData":[TD([[subQ2,-1.0]])],"derivedFrom":subQ0}),1.0]])]});}
            var Q27;
            {var subQ0=sQuery(id+"F0.wireOp",EDGE,"E22");var subQ1=sQuery(id+"F0.wireOp",EDGE,"E1.0");var subQ2=makeQuery(id+"F0.imprint","INTERSECT",VERTEX,{"disambiguationData":[OD(0.0)],"derivedFrom":[subQ1,subQ0]});Q27=makeQuery(id+"F0.imprint","IMPRINT",FACE,{"disambiguationData":[TD([[makeQuery(id+"F0.imprint","IMPRINT",EDGE,{"disambiguationData":[TD([[subQ2,1.0]])],"derivedFrom":subQ0}),1.0]])]});}
            extrude(context, id + "F4", {"entities" : qUnion([Q0, Q1, Q2, Q3, Q4, Q5, Q6, Q7, Q8, Q9, Q10, Q11, Q12, Q13, Q14, Q15, Q16, Q17, Q18, Q19, Q20, Q21, Q22, Q23, Q24, Q25, Q26, Q27]), "operationType" : NewBodyOperationType.ADD, "oppositeDirection" : true, "depth" : 2 * mm});
        }
        {
            var Q0;
            {var subQ3=sQuery(id+"F0.wireOp",EDGE,"E7.2");var subQ7=sQuery(id+"F0.wireOp",EDGE,"E0");var subQ9=makeQuery(id+"F0.imprint","INTERSECT",VERTEX,{"disambiguationData":[OD(0.0)],"derivedFrom":[subQ7,subQ3]});Q0=makeQuery(id+"F0.imprint","IMPRINT",FACE,{"disambiguationData":[TD([[makeQuery(id+"F0.imprint","IMPRINT",EDGE,{"disambiguationData":[TD([[subQ9,-1.0]])],"derivedFrom":subQ7}),1.0]])]});}
            var Q1;
            {var subQ0=sQuery(id+"F0.wireOp",EDGE,"E13");Q1=makeQuery(id+"F0.imprint","IMPRINT",FACE,{"disambiguationData":[TD([[makeQuery(id+"F0.imprint","IMPRINT",EDGE,{"derivedFrom":subQ0}),-1.0]])]});}
            var Q2;
            {var subQ0=sQuery(id+"F0.wireOp",EDGE,"E1.0");var subQ1=makeQuery(id+"F0.imprint","INTERSECT",VERTEX,{"derivedFrom":[subQ0,sQuery(id+"F0.wireOp",EDGE,"E13")]});Q2=makeQuery(id+"F0.imprint","IMPRINT",FACE,{"disambiguationData":[TD([[makeQuery(id+"F0.imprint","IMPRINT",EDGE,{"disambiguationData":[TD([[subQ1,1.0]])],"derivedFrom":subQ0}),-1.0]])]});}
            var Q3;
            {var subQ0=sQuery(id+"F0.wireOp",EDGE,"E7.2");var subQ1=sQuery(id+"F0.wireOp",EDGE,"E0");var subQ2=makeQuery(id+"F0.imprint","INTERSECT",VERTEX,{"disambiguationData":[OD(1.0)],"derivedFrom":[subQ1,subQ0]});Q3=makeQuery(id+"F0.imprint","IMPRINT",FACE,{"disambiguationData":[TD([[makeQuery(id+"F0.imprint","IMPRINT",EDGE,{"disambiguationData":[TD([[subQ2,-1.0]])],"derivedFrom":subQ1}),1.0]])]});}
            var Q4;
            {var subQ5=sQuery(id+"F0.wireOp",EDGE,"E2.right");var subQ6=sQuery(id+"F0.wireOp",EDGE,"E0");var subQ7=makeQuery(id+"F0.imprint","INTERSECT",VERTEX,{"disambiguationData":[OD(1.0)],"derivedFrom":[subQ6,subQ5]});Q4=makeQuery(id+"F0.imprint","IMPRINT",FACE,{"disambiguationData":[TD([[makeQuery(id+"F0.imprint","IMPRINT",EDGE,{"disambiguationData":[TD([[subQ7,-1.0]])],"derivedFrom":subQ6}),1.0]])]});}
            var Q5;
            {var subQ0=sQuery(id+"F0.wireOp",EDGE,"E2.right");var subQ1=sQuery(id+"F0.wireOp",EDGE,"E0");var subQ2=makeQuery(id+"F0.imprint","INTERSECT",VERTEX,{"disambiguationData":[OD(0.0)],"derivedFrom":[subQ1,subQ0]});Q5=makeQuery(id+"F0.imprint","IMPRINT",FACE,{"disambiguationData":[TD([[makeQuery(id+"F0.imprint","IMPRINT",EDGE,{"disambiguationData":[TD([[subQ2,-1.0]])],"derivedFrom":subQ1}),1.0]])]});}
            var Q6;
            {var subQ6=sQuery(id+"F0.wireOp",EDGE,"E0");var subQ11=sQuery(id+"F0.wireOp",EDGE,"E23");var subQ12=makeQuery(id+"F0.imprint","INTERSECT",VERTEX,{"disambiguationData":[OD(1.0)],"derivedFrom":[subQ6,subQ11]});Q6=makeQuery(id+"F0.imprint","IMPRINT",FACE,{"disambiguationData":[TD([[makeQuery(id+"F0.imprint","IMPRINT",EDGE,{"disambiguationData":[TD([[subQ12,-1.0]])],"derivedFrom":subQ6}),1.0]])]});}
            var Q7;
            {var subQ0=sQuery(id+"F0.wireOp",EDGE,"E10");var subQ1=sQuery(id+"F0.wireOp",EDGE,"E1.0");var subQ2=makeQuery(id+"F0.imprint","INTERSECT",VERTEX,{"disambiguationData":[OD(0.0)],"derivedFrom":[subQ1,subQ0]});Q7=makeQuery(id+"F0.imprint","IMPRINT",FACE,{"disambiguationData":[TD([[makeQuery(id+"F0.imprint","IMPRINT",EDGE,{"disambiguationData":[TD([[subQ2,-1.0]])],"derivedFrom":subQ1}),1.0]])]});}
            var Q8;
            {var subQ0=sQuery(id+"F0.wireOp",EDGE,"E23");var subQ1=sQuery(id+"F0.wireOp",EDGE,"E0");var subQ2=makeQuery(id+"F0.imprint","INTERSECT",VERTEX,{"disambiguationData":[OD(0.0)],"derivedFrom":[subQ1,subQ0]});Q8=makeQuery(id+"F0.imprint","IMPRINT",FACE,{"disambiguationData":[TD([[makeQuery(id+"F0.imprint","IMPRINT",EDGE,{"disambiguationData":[TD([[subQ2,-1.0]])],"derivedFrom":subQ1}),1.0]])]});}
            var Q9;
            {var subQ0=sQuery(id+"F0.wireOp",EDGE,"E23");var subQ4=sQuery(id+"F0.wireOp",EDGE,"E1.0");var subQ7=makeQuery(id+"F0.imprint","INTERSECT",VERTEX,{"disambiguationData":[OD(0.0)],"derivedFrom":[subQ4,subQ0]});Q9=makeQuery(id+"F0.imprint","IMPRINT",FACE,{"disambiguationData":[TD([[makeQuery(id+"F0.imprint","IMPRINT",EDGE,{"disambiguationData":[TD([[subQ7,-1.0]])],"derivedFrom":subQ4}),-1.0]])]});}
            var Q10;
            {var subQ5=sQuery(id+"F0.wireOp",EDGE,"E2.left");var subQ6=sQuery(id+"F0.wireOp",EDGE,"E0");var subQ7=makeQuery(id+"F0.imprint","INTERSECT",VERTEX,{"disambiguationData":[OD(0.0)],"derivedFrom":[subQ6,subQ5]});Q10=makeQuery(id+"F0.imprint","IMPRINT",FACE,{"disambiguationData":[TD([[makeQuery(id+"F0.imprint","IMPRINT",EDGE,{"disambiguationData":[TD([[subQ7,-1.0]])],"derivedFrom":subQ6}),1.0]])]});}
            var Q11;
            {var subQ0=sQuery(id+"F0.wireOp",EDGE,"E2.left");var subQ1=sQuery(id+"F0.wireOp",EDGE,"E0");var subQ2=makeQuery(id+"F0.imprint","INTERSECT",VERTEX,{"disambiguationData":[OD(0.0)],"derivedFrom":[subQ1,subQ0]});Q11=makeQuery(id+"F0.imprint","IMPRINT",FACE,{"disambiguationData":[TD([[makeQuery(id+"F0.imprint","IMPRINT",EDGE,{"disambiguationData":[TD([[subQ2,1.0]])],"derivedFrom":subQ1}),1.0]])]});}
            var Q12;
            {var subQ0=sQuery(id+"F0.wireOp",EDGE,"E7.7");var subQ1=sQuery(id+"F0.wireOp",EDGE,"E0");var subQ9=makeQuery(id+"F0.imprint","INTERSECT",VERTEX,{"disambiguationData":[OD(0.0)],"derivedFrom":[subQ1,subQ0]});Q12=makeQuery(id+"F0.imprint","IMPRINT",FACE,{"disambiguationData":[TD([[makeQuery(id+"F0.imprint","IMPRINT",EDGE,{"disambiguationData":[TD([[subQ9,1.0]])],"derivedFrom":subQ1}),1.0]])]});}
            var Q13;
            {var subQ0=sQuery(id+"F0.wireOp",EDGE,"E1.0");var subQ1=makeQuery(id+"F0.imprint","INTERSECT",VERTEX,{"derivedFrom":[subQ0,sQuery(id+"F0.wireOp",EDGE,"E16")]});Q13=makeQuery(id+"F0.imprint","IMPRINT",FACE,{"disambiguationData":[TD([[makeQuery(id+"F0.imprint","IMPRINT",EDGE,{"disambiguationData":[TD([[subQ1,-1.0]])],"derivedFrom":subQ0}),-1.0]])]});}
            var Q14;
            {var subQ0=sQuery(id+"F0.wireOp",EDGE,"E16");Q14=makeQuery(id+"F0.imprint","IMPRINT",FACE,{"disambiguationData":[TD([[makeQuery(id+"F0.imprint","IMPRINT",EDGE,{"derivedFrom":subQ0}),-1.0]])]});}
            var Q15;
            {var subQ0=sQuery(id+"F0.wireOp",EDGE,"E2.left");var subQ1=sQuery(id+"F0.wireOp",EDGE,"E0");var subQ2=makeQuery(id+"F0.imprint","INTERSECT",VERTEX,{"disambiguationData":[OD(1.0)],"derivedFrom":[subQ1,subQ0]});Q15=makeQuery(id+"F0.imprint","IMPRINT",FACE,{"disambiguationData":[TD([[makeQuery(id+"F0.imprint","IMPRINT",EDGE,{"disambiguationData":[TD([[subQ2,-1.0]])],"derivedFrom":subQ1}),1.0]])]});}
            var Q16;
            {var subQ3=sQuery(id+"F0.wireOp",EDGE,"E22");var subQ6=sQuery(id+"F0.wireOp",EDGE,"E0");var subQ9=makeQuery(id+"F0.imprint","INTERSECT",VERTEX,{"disambiguationData":[OD(1.0)],"derivedFrom":[subQ6,subQ3]});Q16=makeQuery(id+"F0.imprint","IMPRINT",FACE,{"disambiguationData":[TD([[makeQuery(id+"F0.imprint","IMPRINT",EDGE,{"disambiguationData":[TD([[subQ9,-1.0]])],"derivedFrom":subQ6}),1.0]])]});}
            var Q17;
            {var subQ0=sQuery(id+"F0.wireOp",EDGE,"E21");var subQ1=sQuery(id+"F0.wireOp",EDGE,"E0");var subQ2=makeQuery(id+"F0.imprint","INTERSECT",VERTEX,{"derivedFrom":[subQ1,subQ0]});Q17=makeQuery(id+"F0.imprint","IMPRINT",FACE,{"disambiguationData":[TD([[makeQuery(id+"F0.imprint","IMPRINT",EDGE,{"disambiguationData":[TD([[subQ2,1.0]])],"derivedFrom":subQ1}),1.0]])]});}
            var Q18;
            {var subQ0=sQuery(id+"F0.wireOp",EDGE,"E21");var subQ1=sQuery(id+"F0.wireOp",EDGE,"E0");var subQ2=makeQuery(id+"F0.imprint","INTERSECT",VERTEX,{"derivedFrom":[subQ1,subQ0]});Q18=makeQuery(id+"F0.imprint","IMPRINT",FACE,{"disambiguationData":[TD([[makeQuery(id+"F0.imprint","IMPRINT",EDGE,{"disambiguationData":[TD([[subQ2,-1.0]])],"derivedFrom":subQ1}),1.0]])]});}
            var Q19;
            {var subQ3=sQuery(id+"F0.wireOp",EDGE,"E21");var subQ5=sQuery(id+"F0.wireOp",EDGE,"E9");var subQ6=makeQuery(id+"F0.imprint","INTERSECT",VERTEX,{"disambiguationData":[OD(1.0)],"derivedFrom":[subQ5,subQ3]});Q19=makeQuery(id+"F0.imprint","IMPRINT",FACE,{"disambiguationData":[TD([[makeQuery(id+"F0.imprint","IMPRINT",EDGE,{"disambiguationData":[TD([[subQ6,-1.0]])],"derivedFrom":subQ5}),1.0]])]});}
            var Q20;
            {var subQ0=sQuery(id+"F0.wireOp",EDGE,"E22");var subQ5=sQuery(id+"F0.wireOp",EDGE,"E9");var subQ7=makeQuery(id+"F0.imprint","INTERSECT",VERTEX,{"disambiguationData":[OD(0.0)],"derivedFrom":[subQ5,subQ0]});Q20=makeQuery(id+"F0.imprint","IMPRINT",FACE,{"disambiguationData":[TD([[makeQuery(id+"F0.imprint","IMPRINT",EDGE,{"disambiguationData":[TD([[subQ7,-1.0]])],"derivedFrom":subQ5}),1.0]])]});}
            var Q21;
            {var subQ1=sQuery(id+"F0.wireOp",EDGE,"E9");var subQ3=sQuery(id+"F0.wireOp",EDGE,"E1.0");var subQ4=makeQuery(id+"F0.imprint","INTERSECT",VERTEX,{"disambiguationData":[OD(0.0)],"derivedFrom":[subQ3,subQ1]});Q21=makeQuery(id+"F0.imprint","IMPRINT",FACE,{"disambiguationData":[TD([[makeQuery(id+"F0.imprint","IMPRINT",EDGE,{"disambiguationData":[TD([[subQ4,-1.0]])],"derivedFrom":subQ3}),1.0]])]});}
            var Q22;
            {var subQ0=sQuery(id+"F0.wireOp",EDGE,"E22");var subQ1=sQuery(id+"F0.wireOp",EDGE,"E1.0");var subQ2=makeQuery(id+"F0.imprint","INTERSECT",VERTEX,{"disambiguationData":[OD(0.0)],"derivedFrom":[subQ1,subQ0]});Q22=makeQuery(id+"F0.imprint","IMPRINT",FACE,{"disambiguationData":[TD([[makeQuery(id+"F0.imprint","IMPRINT",EDGE,{"disambiguationData":[TD([[subQ2,1.0]])],"derivedFrom":subQ0}),1.0]])]});}
            var Q23;
            {var subQ1=sQuery(id+"F0.wireOp",EDGE,"E9");var subQ3=sQuery(id+"F0.wireOp",EDGE,"E1.0");var subQ4=makeQuery(id+"F0.imprint","INTERSECT",VERTEX,{"disambiguationData":[OD(0.0)],"derivedFrom":[subQ3,subQ1]});Q23=makeQuery(id+"F0.imprint","IMPRINT",FACE,{"disambiguationData":[TD([[makeQuery(id+"F0.imprint","IMPRINT",EDGE,{"disambiguationData":[TD([[subQ4,-1.0]])],"derivedFrom":subQ3}),1.0]])]});}
            var Q24;
            {var subQ5=sQuery(id+"F0.wireOp",EDGE,"E1.0");var subQ7=sQuery(id+"F0.wireOp",EDGE,"E22");var subQ9=makeQuery(id+"F0.imprint","INTERSECT",VERTEX,{"disambiguationData":[OD(1.0)],"derivedFrom":[subQ5,subQ7]});Q24=makeQuery(id+"F0.imprint","IMPRINT",FACE,{"disambiguationData":[TD([[makeQuery(id+"F0.imprint","IMPRINT",EDGE,{"disambiguationData":[TD([[subQ9,-1.0]])],"derivedFrom":subQ5}),1.0]])]});}
            var Q25;
            {var subQ0=sQuery(id+"F0.wireOp",EDGE,"E22");var subQ1=sQuery(id+"F0.wireOp",EDGE,"E1.0");var subQ2=makeQuery(id+"F0.imprint","INTERSECT",VERTEX,{"disambiguationData":[OD(1.0)],"derivedFrom":[subQ1,subQ0]});Q25=makeQuery(id+"F0.imprint","IMPRINT",FACE,{"disambiguationData":[TD([[makeQuery(id+"F0.imprint","IMPRINT",EDGE,{"disambiguationData":[TD([[subQ2,-1.0]])],"derivedFrom":subQ1}),-1.0]])]});}
            var Q26;
            {var subQ0=sQuery(id+"F0.wireOp",EDGE,"E22");var subQ1=sQuery(id+"F0.wireOp",EDGE,"E1.0");var subQ2=makeQuery(id+"F0.imprint","INTERSECT",VERTEX,{"disambiguationData":[OD(1.0)],"derivedFrom":[subQ1,subQ0]});Q26=makeQuery(id+"F0.imprint","IMPRINT",FACE,{"disambiguationData":[TD([[makeQuery(id+"F0.imprint","IMPRINT",EDGE,{"disambiguationData":[TD([[subQ2,-1.0]])],"derivedFrom":subQ0}),1.0]])]});}
            var Q27;
            {var subQ0=sQuery(id+"F0.wireOp",EDGE,"E9");var subQ1=sQuery(id+"F0.wireOp",EDGE,"E1.0");var subQ2=makeQuery(id+"F0.imprint","INTERSECT",VERTEX,{"disambiguationData":[OD(0.0)],"derivedFrom":[subQ1,subQ0]});Q27=makeQuery(id+"F0.imprint","IMPRINT",FACE,{"disambiguationData":[TD([[makeQuery(id+"F0.imprint","IMPRINT",EDGE,{"disambiguationData":[TD([[subQ2,-1.0]])],"derivedFrom":subQ1}),-1.0]])]});}
            var Q28;
            {var subQ0=sQuery(id+"F0.wireOp",EDGE,"E14");var subQ1=sQuery(id+"F0.wireOp",EDGE,"E1.0");var subQ2=makeQuery(id+"F0.imprint","INTERSECT",VERTEX,{"derivedFrom":[subQ1,subQ0]});Q28=makeQuery(id+"F0.imprint","IMPRINT",FACE,{"disambiguationData":[TD([[makeQuery(id+"F0.imprint","IMPRINT",EDGE,{"disambiguationData":[TD([[subQ2,-1.0]])],"derivedFrom":subQ1}),1.0]])]});}
            var Q29;
            {var subQ0=sQuery(id+"F0.wireOp",EDGE,"E23");var subQ1=sQuery(id+"F0.wireOp",EDGE,"E1.0");var subQ2=makeQuery(id+"F0.imprint","INTERSECT",VERTEX,{"disambiguationData":[OD(1.0)],"derivedFrom":[subQ1,subQ0]});Q29=makeQuery(id+"F0.imprint","IMPRINT",FACE,{"disambiguationData":[TD([[makeQuery(id+"F0.imprint","IMPRINT",EDGE,{"disambiguationData":[TD([[subQ2,-1.0]])],"derivedFrom":subQ1}),-1.0]])]});}
            var Q30;
            {var subQ0=sQuery(id+"F0.wireOp",EDGE,"E10");var subQ1=sQuery(id+"F0.wireOp",EDGE,"E1.0");var subQ2=makeQuery(id+"F0.imprint","INTERSECT",VERTEX,{"disambiguationData":[OD(0.0)],"derivedFrom":[subQ1,subQ0]});Q30=makeQuery(id+"F0.imprint","IMPRINT",FACE,{"disambiguationData":[TD([[makeQuery(id+"F0.imprint","IMPRINT",EDGE,{"disambiguationData":[TD([[subQ2,-1.0]])],"derivedFrom":subQ1}),-1.0]])]});}
            var Q31;
            {var subQ0=sQuery(id+"F0.wireOp",EDGE,"E23");var subQ1=sQuery(id+"F0.wireOp",EDGE,"E1.0");var subQ2=makeQuery(id+"F0.imprint","INTERSECT",VERTEX,{"disambiguationData":[OD(0.0)],"derivedFrom":[subQ1,subQ0]});Q31=makeQuery(id+"F0.imprint","IMPRINT",FACE,{"disambiguationData":[TD([[makeQuery(id+"F0.imprint","IMPRINT",EDGE,{"disambiguationData":[TD([[subQ2,-1.0]])],"derivedFrom":subQ1}),1.0]])]});}
            var Q32;
            {var subQ0=sQuery(id+"F0.wireOp",EDGE,"E19.MirrorCS");var subQ1=sQuery(id+"F0.wireOp",EDGE,"E1.0");var subQ2=makeQuery(id+"F0.imprint","INTERSECT",VERTEX,{"derivedFrom":[subQ1,subQ0]});Q32=makeQuery(id+"F0.imprint","IMPRINT",FACE,{"disambiguationData":[TD([[makeQuery(id+"F0.imprint","IMPRINT",EDGE,{"disambiguationData":[TD([[subQ2,-1.0]])],"derivedFrom":subQ1}),-1.0]])]});}
            var Q33;
            {var subQ0=sQuery(id+"F0.wireOp",EDGE,"E17.top");var subQ1=sQuery(id+"F0.wireOp",EDGE,"E1.0");var subQ2=makeQuery(id+"F0.imprint","INTERSECT",VERTEX,{"derivedFrom":[subQ1,subQ0]});Q33=makeQuery(id+"F0.imprint","IMPRINT",FACE,{"disambiguationData":[TD([[makeQuery(id+"F0.imprint","IMPRINT",EDGE,{"disambiguationData":[TD([[subQ2,-1.0]])],"derivedFrom":subQ1}),-1.0]])]});}
            extrude(context, id + "F5", {"entities" : qUnion([Q0, Q1, Q2, Q3, Q4, Q5, Q6, Q7, Q8, Q9, Q10, Q11, Q12, Q13, Q14, Q15, Q16, Q17, Q18, Q19, Q20, Q21, Q22, Q23, Q24, Q25, Q26, Q27, Q28, Q29, Q30, Q31, Q32, Q33]), "operationType" : NewBodyOperationType.ADD, "depth" : 10 * mm});
        }
        {
            var Q0;
            Q0=makeQuery(id+"F2.opExtrude","CAP_EDGE",EDGE,{"disambiguationData":[OSD([sQuery(id+"F0.wireOp",EDGE,"E7.2")])],"isStart":false});
            var Q1;
            Q1=makeQuery(id+"F2.opExtrude","CAP_EDGE",EDGE,{"disambiguationData":[OSD([sQuery(id+"F0.wireOp",EDGE,"E7.0")])],"isStart":false});
            var Q2;
            Q2=makeQuery(id+"F2.opExtrude","CAP_EDGE",EDGE,{"disambiguationData":[OSD([sQuery(id+"F0.wireOp",EDGE,"E7.1")])],"isStart":false});
            fillet(context, id + "F6", {"entities" : qUnion([Q0, Q1, Q2]), "radius" : 2 * mm, "tangentPropagation" : true, "allowEdgeOverflow" : false});
        }
        {
            var Q0;
            {var subQ0=sQuery(id+"F0.wireOp",EDGE,"E24");var subQ1=sQuery(id+"F0.wireOp",EDGE,"E7.2");Q0=makeQuery(id+"F4.opExtrude","CAP_EDGE",EDGE,{"disambiguationData":[OSD([subQ0]),TDD([makeQuery(id+"F0.imprint","IMPRINT",EDGE,{"disambiguationData":[TD([[makeQuery(id+"F0.imprint","INTERSECT",VERTEX,{"disambiguationData":[OD(0.0)],"derivedFrom":[subQ1,subQ0]}),1.0]])],"derivedFrom":subQ0})])],"isStart":false});}
            var Q1;
            {var subQ0=sQuery(id+"F0.wireOp",EDGE,"E24");var subQ1=sQuery(id+"F0.wireOp",EDGE,"E7.7");Q1=makeQuery(id+"F4.opExtrude","CAP_EDGE",EDGE,{"disambiguationData":[OSD([subQ0]),TDD([makeQuery(id+"F0.imprint","IMPRINT",EDGE,{"disambiguationData":[TD([[makeQuery(id+"F0.imprint","INTERSECT",VERTEX,{"disambiguationData":[OD(0.0)],"derivedFrom":[subQ1,subQ0]}),-1.0]])],"derivedFrom":subQ0})])],"isStart":false});}
            fillet(context, id + "F7", {"entities" : qUnion([Q0, Q1]), "radius" : 2 * mm, "tangentPropagation" : true, "allowEdgeOverflow" : false});
        }
        {
            var Q0;
            Q0=makeQuery(id+"F2.opExtrude","CAP_EDGE",EDGE,{"disambiguationData":[OSD([sQuery(id+"F0.wireOp",EDGE,"E7.5")])],"isStart":true});
            var Q1;
            Q1=makeQuery(id+"F2.opExtrude","CAP_EDGE",EDGE,{"disambiguationData":[OSD([sQuery(id+"F0.wireOp",EDGE,"E7.4")])],"isStart":true});
            var Q2;
            {var subQ0=sQuery(id+"F0.wireOp",EDGE,"E7.2");var subQ5=sQuery(id+"F0.wireOp",EDGE,"E7.4");Q2=makeQuery(id+"F4.boolean.opBoolean","SPLIT",EDGE,{"disambiguationData":[TD([makeQuery(id+"F2.opExtrude","SWEPT_FACE",FACE,{"disambiguationData":[OSD([subQ5])]})])],"derivedFrom":makeQuery(id+"F2.opExtrude","CAP_EDGE",EDGE,{"disambiguationData":[OSD([subQ0])],"isStart":true})});}
            var Q3;
            Q3=makeQuery(id+"F2.opExtrude","CAP_EDGE",EDGE,{"disambiguationData":[OSD([sQuery(id+"F0.wireOp",EDGE,"E7.1")])],"isStart":true});
            fillet(context, id + "F8", {"entities" : qUnion([Q0, Q1, Q2, Q3]), "radius" : 2 * mm, "tangentPropagation" : true, "allowEdgeOverflow" : false});
        }
    });
